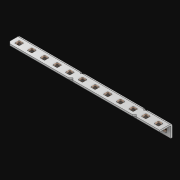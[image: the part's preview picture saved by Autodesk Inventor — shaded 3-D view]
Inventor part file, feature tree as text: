
AUTODESK INVENTOR PART (.ipt)
format: ipt  version: 2021 (Build 250183000, 183)  size: 642,560 bytes
history: native  units: in
note: dims shown in document units (in); Inventor stores cm internally (conversion verified against a paired STEP export)
features: extrude x25, other x24, sketch x3, pattern_linear x1, sheet_metal_op x1
ambient origin geometry x8: Origin, YZ Plane, XZ Plane, XY Plane, X Axis, Y Axis, Z Axis, Center Point
bodies: Solid1 (feature_tree)
feature tree (54):
  pattern_linear  "Rectangular Pattern1"  Spacing1=0.063in  [1 undecoded]
  extrude  "Extrusion1"  Depth=0.5in
  sketch  "Sketch1"  dims[d0=0.182in]
  other  "Srf1"
  sketch  "Sketch2"  dims[d1=0.063in d2=0.0in]
  other  "Srf2"
  other  "Srf3"
  other  "Srf5"
  other  "Srf7"
  other  "Srf9"
  other  "Srf11"
  other  "Srf13"
  other  "Srf15"
  other  "Srf17"
  other  "Srf19"
  other  "Srf21"
  other  "Srf23"
  other  "Srf4"
  other  "Srf6"
  other  "Srf8"
  other  "Srf10"
  other  "Srf12"
  other  "Srf14"
  other  "Srf16"
  other  "Srf18"
  other  "Srf20"
  other  "Srf22"
  other  "Srf24"
  sketch  "Sketch3"  dims[d3=0.182in d4=0.063in d5=0.0in d8=0.5in d9=11.5in d10=0.0in]
  sheet_metal_op  "Fold1"
  extrude  "ExtrusionSrf1"  Depth=0.5in TaperAngle=0.0deg
  extrude  "ExtrusionSrf2"  [1 undecoded]
  extrude  "ExtrusionSrf3"  [1 undecoded]
  extrude  "ExtrusionSrf4"  [1 undecoded]
  extrude  "ExtrusionSrf5"  [1 undecoded]
  extrude  "ExtrusionSrf6"  [1 undecoded]
  extrude  "ExtrusionSrf7"  [1 undecoded]
  extrude  "ExtrusionSrf8"  [1 undecoded]
  extrude  "ExtrusionSrf9"  [1 undecoded]
  extrude  "ExtrusionSrf10"  [1 undecoded]
  extrude  "ExtrusionSrf11"  [1 undecoded]
  extrude  "ExtrusionSrf12"  [1 undecoded]
  extrude  "ExtrusionSrf13"  [1 undecoded]
  extrude  "ExtrusionSrf37"  [1 undecoded]
  extrude  "ExtrusionSrf38"  [1 undecoded]
  extrude  "ExtrusionSrf39"  [1 undecoded]
  extrude  "ExtrusionSrf40"  [1 undecoded]
  extrude  "ExtrusionSrf41"  [1 undecoded]
  extrude  "ExtrusionSrf42"  [1 undecoded]
  extrude  "ExtrusionSrf43"  [1 undecoded]
  extrude  "ExtrusionSrf44"  [1 undecoded]
  extrude  "ExtrusionSrf45"  [1 undecoded]
  extrude  "ExtrusionSrf46"  [1 undecoded]
  extrude  "ExtrusionSrf47"  [1 undecoded]
note: 24 required parameter values undecoded (feature->parameter linkage not recoverable at this tier; creation-order binding heuristic only, values carry confidence <= 0.55)
